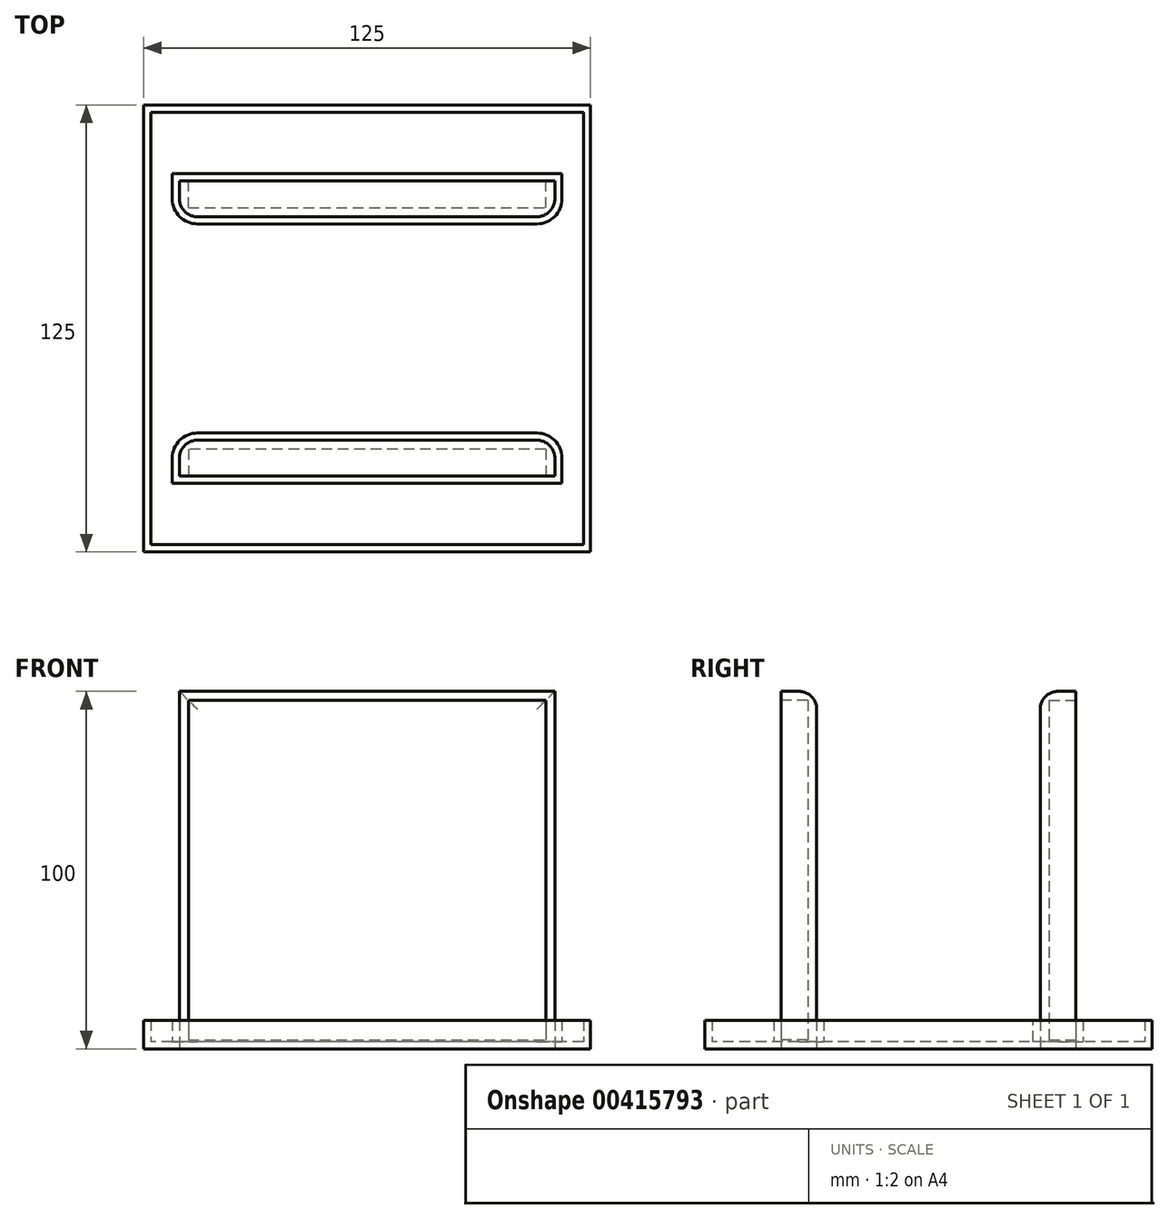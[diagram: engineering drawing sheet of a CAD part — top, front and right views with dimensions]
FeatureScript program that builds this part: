
annotation { "Feature Type Name" : "Feature", "Feature Type Description" : "" }
export const myFeature = defineFeature(function(context is Context, id is Id, definition is map)
    precondition{}
    {
        {
            var Q0;
            Q0=qCreatedBy(makeId("Top.planeOp"),FACE);
            var sketch = newSketch(context, id + "F0", { "sketchPlane" : qUnion([Q0])});
            skLineSegment(sketch, "E0.bottom", {"start": v(62.5, 62.5) * mm, "end": v(-62.5, 62.5) * mm});
            skLineSegment(sketch, "E0.top", {"start": v(62.5, -62.5) * mm, "end": v(-62.5, -62.5) * mm});
            skLineSegment(sketch, "E0.left", {"start": v(62.5, 62.5) * mm, "end": v(62.5, -62.5) * mm});
            skLineSegment(sketch, "E0.right", {"start": v(-62.5, 62.5) * mm, "end": v(-62.5, -62.5) * mm});
            skPoint(sketch, "E0.middle", {"position": v(0, 0) * mm});
            skLineSegment(sketch, "E1", {"start": v(-62.5, 0) * mm, "end": v(0, 0) * mm, "construction": true});
            skLineSegment(sketch, "E2", {"start": v(0, 62.5) * mm, "end": v(0, 0) * mm, "construction": true});
            skLineSegment(sketch, "E3", {"start": v(0, 0) * mm, "end": v(62.5, 0) * mm, "construction": true});
            skLineSegment(sketch, "E4", {"start": v(0, 0) * mm, "end": v(0, -62.5) * mm, "construction": true});
            skLineSegment(sketch, "E5.bottom", {"start": v(0, 31.25) * mm, "end": v(52.5, 31.25) * mm});
            skLineSegment(sketch, "E5.top", {"start": v(0, 41.25) * mm, "end": v(52.5, 41.25) * mm});
            skLineSegment(sketch, "E5.right", {"start": v(52.5, 31.25) * mm, "end": v(52.5, 41.25) * mm});
            skLineSegment(sketch, "E6.MirrorCS", {"start": v(0, 31.25) * mm, "end": v(-52.5, 31.25) * mm});
            skLineSegment(sketch, "E7.MirrorCS", {"start": v(-52.5, 31.25) * mm, "end": v(-52.5, 41.25) * mm});
            skLineSegment(sketch, "E8.MirrorCS", {"start": v(0, 41.25) * mm, "end": v(-52.5, 41.25) * mm});
            skLineSegment(sketch, "E9.MirrorCS", {"start": v(0, -31.25) * mm, "end": v(52.5, -31.25) * mm});
            skLineSegment(sketch, "E10.MirrorCS", {"start": v(0, -41.25) * mm, "end": v(-52.5, -41.25) * mm});
            skLineSegment(sketch, "E11.MirrorCS", {"start": v(-52.5, -31.25) * mm, "end": v(-52.5, -41.25) * mm});
            skLineSegment(sketch, "E12.MirrorCS", {"start": v(0, -31.25) * mm, "end": v(-52.5, -31.25) * mm});
            skLineSegment(sketch, "E13.MirrorCS", {"start": v(52.5, -31.25) * mm, "end": v(52.5, -41.25) * mm});
            skLineSegment(sketch, "E14.MirrorCS", {"start": v(0, -41.25) * mm, "end": v(52.5, -41.25) * mm});
            skSolve(sketch);
        }
        {
            var Q0;
            Q0=makeQuery(id+"F0.imprint","IMPRINT",FACE,{"disambiguationData":[TD([[makeQuery(id+"F0.imprint","IMPRINT",EDGE,{"derivedFrom":sQuery(id+"F0.wireOp",EDGE,"E0.bottom")}),1.0]])]});
            extrude(context, id + "F1", {"entities" : qUnion([Q0]), "depth" : 8 * mm});
        }
        {
            var Q0;
            Q0=makeQuery(id+"F0.imprint","IMPRINT",FACE,{"disambiguationData":[TD([[makeQuery(id+"F0.imprint","IMPRINT",EDGE,{"derivedFrom":sQuery(id+"F0.wireOp",EDGE,"E9.MirrorCS")}),-1.0]])]});
            var Q1;
            Q1=makeQuery(id+"F0.imprint","IMPRINT",FACE,{"disambiguationData":[TD([[makeQuery(id+"F0.imprint","IMPRINT",EDGE,{"derivedFrom":sQuery(id+"F0.wireOp",EDGE,"E5.bottom")}),1.0]])]});
            extrude(context, id + "F2", {"entities" : qUnion([Q0, Q1]), "depth" : 100 * mm});
        }
        {
            var Q0;
            Q0=makeQuery(id+"F2.opExtrude","SWEPT_FACE",FACE,{"disambiguationData":[OSD([sQuery(id+"F0.wireOp",EDGE,"E5.top"),sQuery(id+"F0.wireOp",EDGE,"E8.MirrorCS")])]});
            var Q1;
            Q1=makeQuery(id+"F2.opExtrude","SWEPT_FACE",FACE,{"disambiguationData":[OSD([sQuery(id+"F0.wireOp",EDGE,"E10.MirrorCS"),sQuery(id+"F0.wireOp",EDGE,"E14.MirrorCS")])]});
            shell(context, id + "F3", {"entities" : qUnion([Q0, Q1]), "thickness" : 2.5 * mm});
        }
        {
            var Q0;
            Q0=makeQuery(id+"F2.opExtrude","SWEPT_EDGE",EDGE,{"disambiguationData":[OSD([sQuery(id+"F0.wireOp",EDGE,"E6.MirrorCS"),sQuery(id+"F0.wireOp",EDGE,"E7.MirrorCS")])]});
            var Q1;
            Q1=makeQuery(id+"F2.opExtrude","CAP_EDGE",EDGE,{"disambiguationData":[OSD([sQuery(id+"F0.wireOp",EDGE,"E5.bottom"),sQuery(id+"F0.wireOp",EDGE,"E6.MirrorCS")])],"isStart":false});
            var Q2;
            Q2=makeQuery(id+"F2.opExtrude","SWEPT_EDGE",EDGE,{"disambiguationData":[OSD([sQuery(id+"F0.wireOp",EDGE,"E5.bottom"),sQuery(id+"F0.wireOp",EDGE,"E5.right")])]});
            var Q3;
            Q3=makeQuery(id+"F2.opExtrude","SWEPT_EDGE",EDGE,{"disambiguationData":[OSD([sQuery(id+"F0.wireOp",EDGE,"E11.MirrorCS"),sQuery(id+"F0.wireOp",EDGE,"E12.MirrorCS")])]});
            var Q4;
            Q4=makeQuery(id+"F2.opExtrude","CAP_EDGE",EDGE,{"disambiguationData":[OSD([sQuery(id+"F0.wireOp",EDGE,"E9.MirrorCS"),sQuery(id+"F0.wireOp",EDGE,"E12.MirrorCS")])],"isStart":false});
            var Q5;
            Q5=makeQuery(id+"F2.opExtrude","SWEPT_EDGE",EDGE,{"disambiguationData":[OSD([sQuery(id+"F0.wireOp",EDGE,"E9.MirrorCS"),sQuery(id+"F0.wireOp",EDGE,"E13.MirrorCS")])]});
            fillet(context, id + "F4", {"entities" : qUnion([Q0, Q1, Q2, Q3, Q4, Q5]), "radius" : 5 * mm, "tangentPropagation" : true, "allowEdgeOverflow" : false});
        }
        {
            var Q0;
            Q0=makeQuery(id+"F1.opExtrude","SWEPT_EDGE",EDGE,{"disambiguationData":[OSD([sQuery(id+"F0.wireOp",EDGE,"E5.bottom"),sQuery(id+"F0.wireOp",EDGE,"E5.right")])]});
            var Q1;
            Q1=makeQuery(id+"F1.opExtrude","SWEPT_EDGE",EDGE,{"disambiguationData":[OSD([sQuery(id+"F0.wireOp",EDGE,"E6.MirrorCS"),sQuery(id+"F0.wireOp",EDGE,"E7.MirrorCS")])]});
            var Q2;
            Q2=makeQuery(id+"F1.opExtrude","SWEPT_EDGE",EDGE,{"disambiguationData":[OSD([sQuery(id+"F0.wireOp",EDGE,"E11.MirrorCS"),sQuery(id+"F0.wireOp",EDGE,"E12.MirrorCS")])]});
            var Q3;
            Q3=makeQuery(id+"F1.opExtrude","SWEPT_EDGE",EDGE,{"disambiguationData":[OSD([sQuery(id+"F0.wireOp",EDGE,"E9.MirrorCS"),sQuery(id+"F0.wireOp",EDGE,"E13.MirrorCS")])]});
            fillet(context, id + "F5", {"entities" : qUnion([Q0, Q1, Q2, Q3]), "radius" : 5 * mm, "tangentPropagation" : true, "allowEdgeOverflow" : false});
        }
        {
            var Q0;
            Q0=makeQuery(id+"F1.opExtrude","CAP_FACE",FACE,{"disambiguationData":[OSD([sQuery(id+"F0.wireOp",EDGE,"E0.bottom"),sQuery(id+"F0.wireOp",EDGE,"E0.top"),sQuery(id+"F0.wireOp",EDGE,"E0.left"),sQuery(id+"F0.wireOp",EDGE,"E0.right"),sQuery(id+"F0.wireOp",EDGE,"E5.bottom"),sQuery(id+"F0.wireOp",EDGE,"E5.top"),sQuery(id+"F0.wireOp",EDGE,"E5.right"),sQuery(id+"F0.wireOp",EDGE,"E6.MirrorCS"),sQuery(id+"F0.wireOp",EDGE,"E7.MirrorCS"),sQuery(id+"F0.wireOp",EDGE,"E8.MirrorCS"),sQuery(id+"F0.wireOp",EDGE,"E9.MirrorCS"),sQuery(id+"F0.wireOp",EDGE,"E10.MirrorCS"),sQuery(id+"F0.wireOp",EDGE,"E11.MirrorCS"),sQuery(id+"F0.wireOp",EDGE,"E12.MirrorCS"),sQuery(id+"F0.wireOp",EDGE,"E13.MirrorCS"),sQuery(id+"F0.wireOp",EDGE,"E14.MirrorCS")])],"isStart":false});
            shell(context, id + "F6", {"entities" : qUnion([Q0]), "thickness" : 2 * mm});
        }
    });
